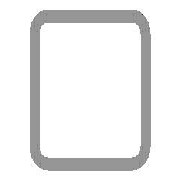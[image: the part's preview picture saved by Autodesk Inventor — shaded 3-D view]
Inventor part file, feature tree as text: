
AUTODESK INVENTOR PART (.ipt)
format: ipt  version: 2025 (Build 290162010, 162A)  size: 142,336 bytes
history: native  units: mm (DEFAULTED — no unit token found)
features: other x4, sketch x1, plane x1
ambient origin geometry x8: Origin, YZ Plane, XZ Plane, XY Plane, X Axis, Y Axis, Z Axis, Center Point
bodies: Solid1 (feature_tree), Body (feature_tree)
feature tree (6):
  parser-record x1  (decoder bookkeeping rows leaked as tree rows — omitted from the tree; the rows remain in map.json)
  other  "Driven Length"
  other  "Start Plane"
  other  "End Plane"
  sketch  "Sketch3"  dims[d3=2870.0mm d4=0.0mm d7=6.0mm d9=80.0mm d11=80.0mm d12=3.0mm d13=-0.0mm d14=2870.0mm d15=40.0mm d16=40.0mm d17=90.0deg d18=2870.0mm]
  plane  "Work Plane3"
